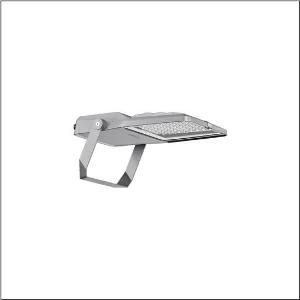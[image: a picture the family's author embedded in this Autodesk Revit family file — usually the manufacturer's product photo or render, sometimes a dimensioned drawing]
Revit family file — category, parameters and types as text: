
# Revit family: floodlight_fl_21_mini___pl52_5xa7776b2d1a_de24
name_source: partatom
category: Lighting Fixtures
units: mm (PartAtom-declared; Revit-internal decimal feet)

## family parameters
Cut with Voids When Loaded = No
Host = Face
Light Source = No
Part Type = Normal
Room Calculation Point = No
Round Connector Dimension = Use Diameter
Shared = No

## types (1)
- --- (1 x LED, 6230 lm, 45.7 W, 3000K)
    Apparent Load = 46 VA
    CIE Flux Codes = 26 60 98 100 100
    Color Rendering = 70
    Color Temperature = 3000K
    Default Elevation = 1800 mm
    Description = Floodlight FL 21 mini, floodlight, primary light control with lens, of PMMA, primary optical cover: protective disc, of toughened safety glass, transparent, light distribution: PL52, light emission: direct distribution, installation type: surface-mounted, LED, High Power LED, rated luminous flux: 6.230lm, luminous efficacy: 136lm/W, light colour: 730, colour temperature: 3000K, control: flexible luminous flux parameterisation, time-dependent luminous flux control, constant luminous flux control, overheat protection, presetting dimming logarithmic, with terminal, 6-pole, mains connection: 220..240V, AC, 50/60Hz, start of lifetime: 46W, end of service life: 48W, reduction: 22W, luminaire housing, of diecast aluminium, powder-coated, Siteco® metallic grey (DB 702S), corrosivity category C5 mid according to DIN EN ISO 12944, sealing non-destructively replaceable, mounting bracket, of steel, galvanised, powder-coated, Siteco® metallic grey (DB 702S), Smart Interface below and above, protection rating (complete): IP66, insulation class (complete): insulation class II (safety insulation), certification: CE, ENEC, VDE, protection symbol: D, impact resistance: IK08, permissible operating ambient temperature: -40..+40°C, permissible operating ambient temperature for outdoor applications: -40..+50°C, standard: DIN EN 12944, LABS conformity tested according to VDMA 24364:2018-05, packaging unit: 1 piece

Light Distribution: PL52
    Height = 70 mm
    Lamp = 1 x LED
    Lamp Light Flux = 6230 lm
    Lamp Power = 45.7 W
    Lamp count = 1
    Length = 485 mm
    Luminous efficacy = 136 lm/W
    Manufacturer = Siteco
    ModVariant = No
    Model = 5XA7776B2D1A
    Number of Poles = 1
    OnlyDefault = Yes
    Power Factor = 1
    Product Name = Floodlight FL 21 mini | PL52
    Product group = floodlight | pylon annexe
    ProductGroupID = 6200
    Protection Class = Protection class II
    Protection Degree = IP 66
    RLX_Detail_Level = 1
    RLX_Emergency_Light_Flux = 0 lm
    RLX_Emergency_Type = 0
    RLX_Emergency_Type_DB = No
    RlxData = <blob elided: 96021 chars, md5=249bcb25>
    Socket = socket
    Standby Power = 0 W
    System Light Flux = 6230 lm
    System Power = 46 W
    Type Comments = factory setting: luminous flux: 100 % | dim-lin: 254 | 463 mA
    Type Image = l_1006845.jpg
    URL = http://relux.com
    VarID = @adj_113571
    Voltage = 0 V
    Weight = 0.00 kg
    Width = 337 mm

## geometry (parser evidence)
native form markers: Blend x4, Sweep x12
no freeform markers — native parametric forms only
